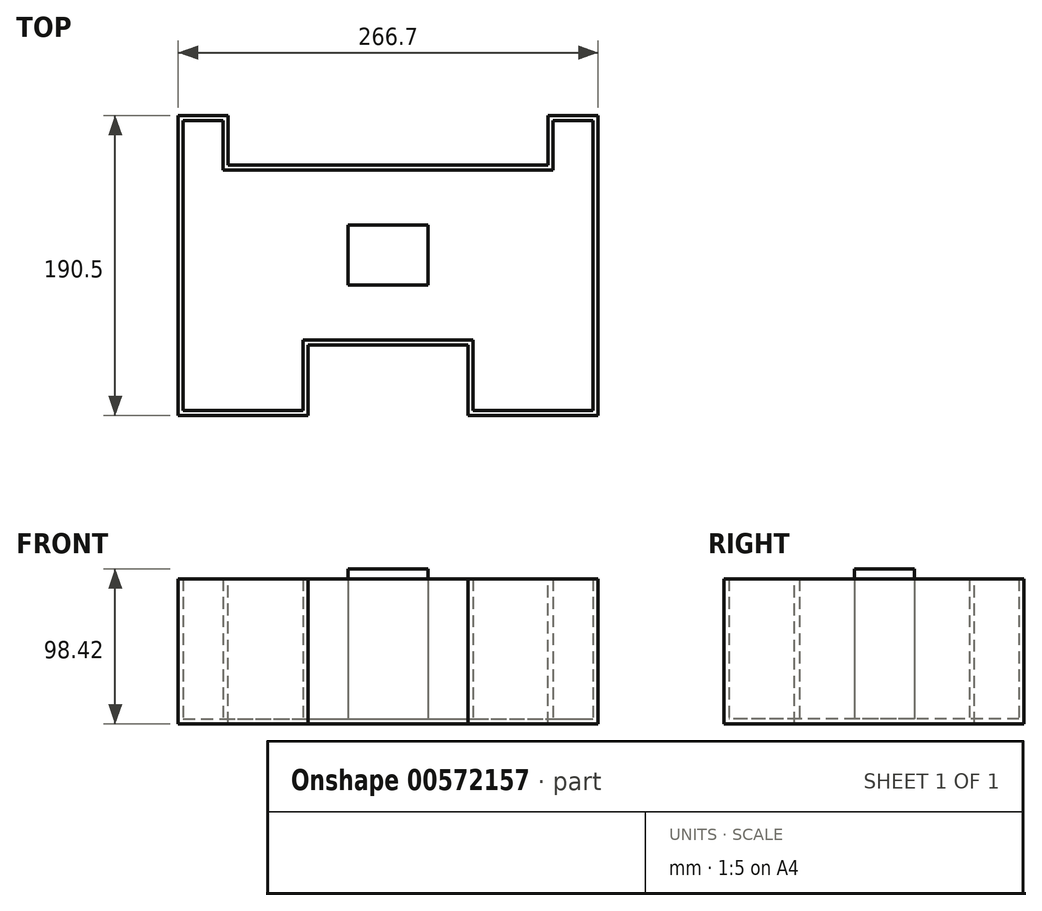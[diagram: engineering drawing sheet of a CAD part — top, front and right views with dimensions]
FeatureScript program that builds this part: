
annotation { "Feature Type Name" : "Feature", "Feature Type Description" : "" }
export const myFeature = defineFeature(function(context is Context, id is Id, definition is map)
    precondition{}
    {
        {
            var Q0;
            Q0=qCreatedBy(makeId("Top.planeOp"),FACE);
            var sketch = newSketch(context, id + "F0", { "sketchPlane" : qUnion([Q0])});
            skLineSegment(sketch, "E0.bottom", {"start": v(-169.86, 103.29) * mm, "end": v(-138.1, 103.29) * mm});
            skLineSegment(sketch, "E0.top", {"start": v(-169.86, -87.21) * mm, "end": v(-87.3, -87.21) * mm});
            skLineSegment(sketch, "E0.left", {"start": v(-169.86, 103.29) * mm, "end": v(-169.86, -87.21) * mm});
            skLineSegment(sketch, "E0.right", {"start": v(96.84, 103.29) * mm, "end": v(96.84, -87.21) * mm});
            skLineSegment(sketch, "E1.top", {"start": v(-138.1, 71.8) * mm, "end": v(65.1, 71.8) * mm});
            skLineSegment(sketch, "E1.left", {"start": v(-138.1, 103.29) * mm, "end": v(-138.1, 71.8) * mm});
            skLineSegment(sketch, "E1.right", {"start": v(65.1, 103.29) * mm, "end": v(65.1, 71.8) * mm});
            skLineSegment(sketch, "E2.bottom", {"start": v(-87.3, -42.5) * mm, "end": v(14.3, -42.5) * mm});
            skLineSegment(sketch, "E2.left", {"start": v(-87.3, -42.5) * mm, "end": v(-87.3, -87.21) * mm});
            skLineSegment(sketch, "E2.right", {"start": v(14.3, -42.5) * mm, "end": v(14.3, -87.21) * mm});
            skLineSegment(sketch, "E3.trimOffspring", {"start": v(14.3, -87.21) * mm, "end": v(96.84, -87.21) * mm});
            skLineSegment(sketch, "E4.trimOffspring", {"start": v(65.1, 103.29) * mm, "end": v(96.84, 103.29) * mm});
            skSolve(sketch);
        }
        {
            var Q0;
            Q0=makeQuery(id+"F0.imprint","IMPRINT",FACE,{"disambiguationData":[TD([[makeQuery(id+"F0.imprint","IMPRINT",EDGE,{"derivedFrom":sQuery(id+"F0.wireOp",EDGE,"E0.bottom")}),-1.0]])]});
            extrude(context, id + "F1", {"entities" : qUnion([Q0]), "oppositeDirection" : true, "depth" : 3.17 * mm, "offsetDistance" : 25.4 * mm});
        }
        {
            var Q0;
            Q0=makeQuery(id+"F1.opExtrude","CAP_FACE",FACE,{"disambiguationData":[OSD([sQuery(id+"F0.wireOp",EDGE,"E0.bottom"),sQuery(id+"F0.wireOp",EDGE,"E0.top"),sQuery(id+"F0.wireOp",EDGE,"E0.left"),sQuery(id+"F0.wireOp",EDGE,"E0.right"),sQuery(id+"F0.wireOp",EDGE,"E1.top"),sQuery(id+"F0.wireOp",EDGE,"E1.left"),sQuery(id+"F0.wireOp",EDGE,"E1.right"),sQuery(id+"F0.wireOp",EDGE,"E2.bottom"),sQuery(id+"F0.wireOp",EDGE,"E2.left"),sQuery(id+"F0.wireOp",EDGE,"E2.right"),sQuery(id+"F0.wireOp",EDGE,"E3.trimOffspring"),sQuery(id+"F0.wireOp",EDGE,"E4.trimOffspring")])],"isStart":true});
            var sketch = newSketch(context, id + "F2", { "sketchPlane" : qUnion([Q0])});
            skLineSegment(sketch, "E5.bottom", {"start": v(-166.68, 100.11) * mm, "end": v(-141.28, 100.11) * mm});
            skLineSegment(sketch, "E5.top", {"start": v(-166.68, -84.04) * mm, "end": v(-116.96, -84.04) * mm});
            skLineSegment(sketch, "E5.left", {"start": v(-166.68, 100.11) * mm, "end": v(-166.68, -84.04) * mm});
            skLineSegment(sketch, "E5.right", {"start": v(-141.28, 100.11) * mm, "end": v(-141.28, 68.63) * mm});
            skLineSegment(sketch, "E6.bottom", {"start": v(-141.28, 68.63) * mm, "end": v(68.27, 68.63) * mm});
            skLineSegment(sketch, "E6.top", {"start": v(-90.48, -39.32) * mm, "end": v(17.47, -39.32) * mm});
            skLineSegment(sketch, "E7.bottom", {"start": v(68.27, 100.11) * mm, "end": v(93.67, 100.11) * mm});
            skLineSegment(sketch, "E7.top", {"start": v(40.34, -84.04) * mm, "end": v(93.67, -84.04) * mm});
            skLineSegment(sketch, "E7.left", {"start": v(68.27, 100.11) * mm, "end": v(68.27, 68.63) * mm});
            skLineSegment(sketch, "E7.right", {"start": v(93.67, 100.11) * mm, "end": v(93.67, -84.04) * mm});
            skLineSegment(sketch, "E8", {"start": v(-116.96, -84.04) * mm, "end": v(-90.48, -84.04) * mm});
            skLineSegment(sketch, "E9", {"start": v(-90.48, -84.04) * mm, "end": v(-90.48, -39.32) * mm});
            skLineSegment(sketch, "E10", {"start": v(17.47, -39.32) * mm, "end": v(17.47, -84.04) * mm});
            skLineSegment(sketch, "E11", {"start": v(17.47, -84.04) * mm, "end": v(40.34, -84.04) * mm});
            skLineSegment(sketch, "E12", {"start": v(-169.86, 103.29) * mm, "end": v(-138.1, 103.29) * mm});
            skLineSegment(sketch, "E13", {"start": v(-138.1, 103.29) * mm, "end": v(-138.1, 71.8) * mm});
            skLineSegment(sketch, "E14", {"start": v(-138.1, 71.8) * mm, "end": v(65.1, 71.8) * mm});
            skLineSegment(sketch, "E15", {"start": v(65.1, 71.8) * mm, "end": v(65.1, 103.29) * mm});
            skLineSegment(sketch, "E16", {"start": v(65.1, 103.29) * mm, "end": v(96.84, 103.29) * mm});
            skLineSegment(sketch, "E17", {"start": v(96.84, 103.29) * mm, "end": v(96.84, -87.21) * mm});
            skLineSegment(sketch, "E18", {"start": v(96.84, -87.21) * mm, "end": v(14.3, -87.21) * mm});
            skLineSegment(sketch, "E19", {"start": v(14.3, -87.21) * mm, "end": v(14.3, -42.5) * mm});
            skLineSegment(sketch, "E20", {"start": v(14.3, -42.5) * mm, "end": v(-87.3, -42.5) * mm});
            skLineSegment(sketch, "E21", {"start": v(-87.3, -42.5) * mm, "end": v(-87.3, -87.21) * mm});
            skLineSegment(sketch, "E22", {"start": v(-87.3, -87.21) * mm, "end": v(-169.86, -87.21) * mm});
            skLineSegment(sketch, "E23", {"start": v(-169.86, -87.21) * mm, "end": v(-169.86, 103.29) * mm});
            skSolve(sketch);
        }
        {
            var Q0;
            Q0=makeQuery(id+"F2.imprint","IMPRINT",FACE,{"disambiguationData":[TD([[makeQuery(id+"F2.imprint","IMPRINT",EDGE,{"derivedFrom":sQuery(id+"F2.wireOp",EDGE,"E5.bottom")}),1.0]])]});
            extrude(context, id + "F3", {"entities" : qUnion([Q0]), "operationType" : NewBodyOperationType.ADD, "depth" : 88.9 * mm, "offsetDistance" : 25.4 * mm});
        }
        {
            var Q0;
            Q0=makeQuery(id+"F1.opExtrude","CAP_FACE",FACE,{"disambiguationData":[OSD([sQuery(id+"F0.wireOp",EDGE,"E0.bottom"),sQuery(id+"F0.wireOp",EDGE,"E0.top"),sQuery(id+"F0.wireOp",EDGE,"E0.left"),sQuery(id+"F0.wireOp",EDGE,"E0.right"),sQuery(id+"F0.wireOp",EDGE,"E1.top"),sQuery(id+"F0.wireOp",EDGE,"E1.left"),sQuery(id+"F0.wireOp",EDGE,"E1.right"),sQuery(id+"F0.wireOp",EDGE,"E2.bottom"),sQuery(id+"F0.wireOp",EDGE,"E2.left"),sQuery(id+"F0.wireOp",EDGE,"E2.right"),sQuery(id+"F0.wireOp",EDGE,"E3.trimOffspring"),sQuery(id+"F0.wireOp",EDGE,"E4.trimOffspring")])],"isStart":true});
            var sketch = newSketch(context, id + "F4", { "sketchPlane" : qUnion([Q0])});
            skLineSegment(sketch, "E24.bottom", {"start": v(-61.9, 33.7) * mm, "end": v(-11.1, 33.7) * mm});
            skLineSegment(sketch, "E24.top", {"start": v(-61.9, -4.4) * mm, "end": v(-11.1, -4.4) * mm});
            skLineSegment(sketch, "E24.left", {"start": v(-61.9, 33.7) * mm, "end": v(-61.9, -4.4) * mm});
            skLineSegment(sketch, "E24.right", {"start": v(-11.1, 33.7) * mm, "end": v(-11.1, -4.4) * mm});
            skSolve(sketch);
        }
        {
            var Q0;
            Q0 = qSketchRegion(id + "F4", true);
            extrude(context, id + "F5", {"entities" : qUnion([Q0]), "operationType" : NewBodyOperationType.ADD, "depth" : 95.25 * mm, "offsetDistance" : 25.4 * mm});
        }
    });
